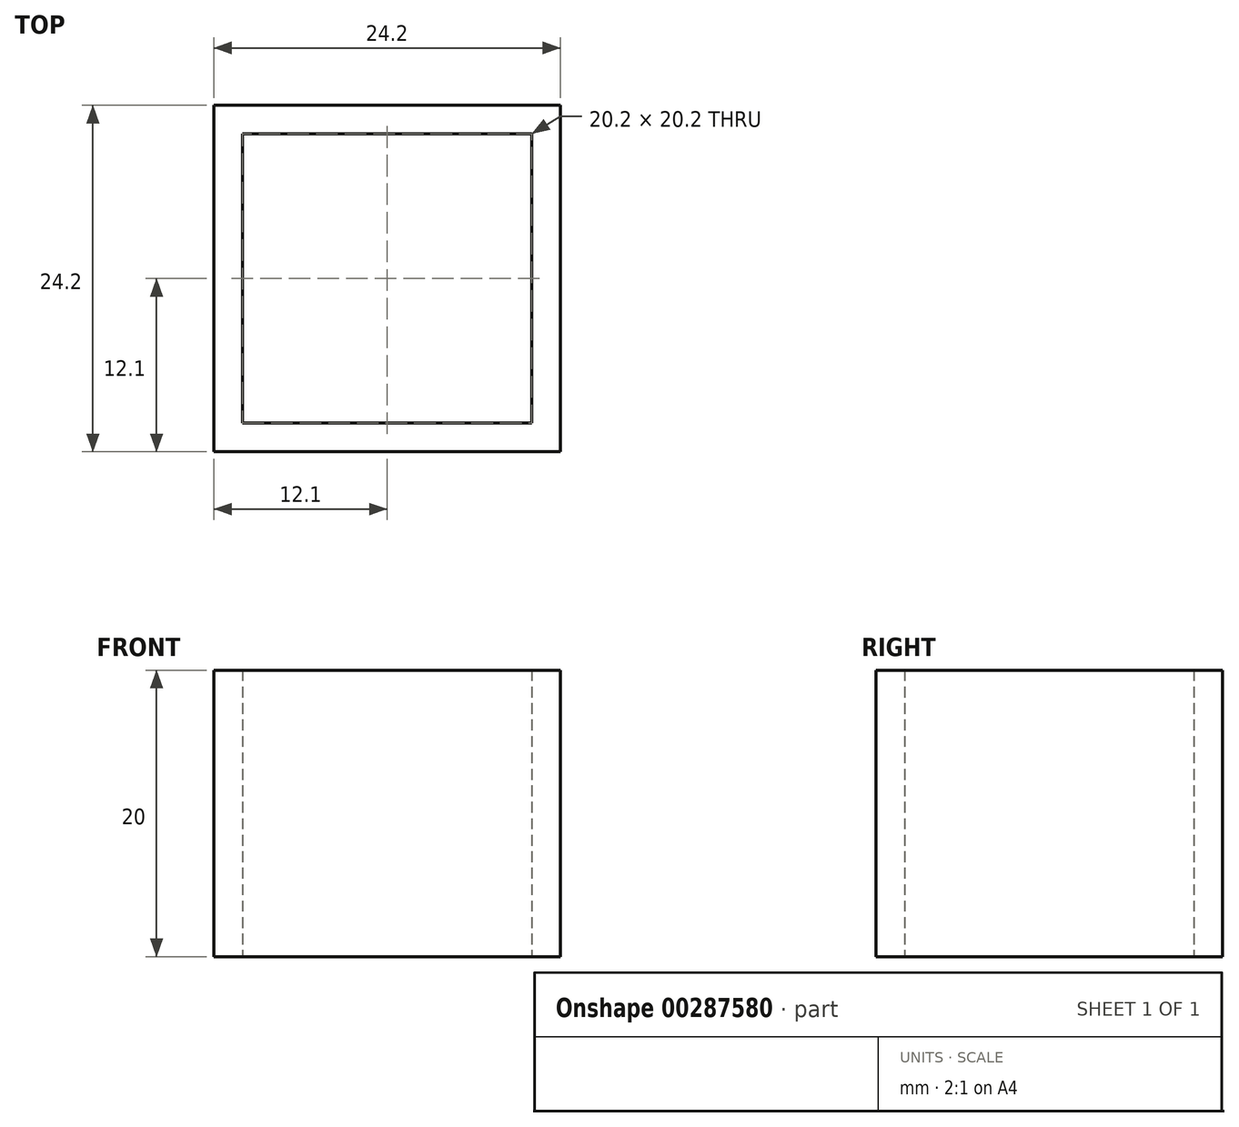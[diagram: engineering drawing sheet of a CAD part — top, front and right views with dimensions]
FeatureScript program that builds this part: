
annotation { "Feature Type Name" : "Feature", "Feature Type Description" : "" }
export const myFeature = defineFeature(function(context is Context, id is Id, definition is map)
    precondition{}
    {
        {
            var Q0;
            Q0=qCreatedBy(makeId("Top.planeOp"),FACE);
            var sketch = newSketch(context, id + "F0", { "sketchPlane" : qUnion([Q0])});
            skLineSegment(sketch, "E0.bottom", {"start": v(10.1, -10.1) * mm, "end": v(-10.1, -10.1) * mm});
            skLineSegment(sketch, "E0.top", {"start": v(10.1, 10.1) * mm, "end": v(-10.1, 10.1) * mm});
            skLineSegment(sketch, "E0.left", {"start": v(10.1, -10.1) * mm, "end": v(10.1, 10.1) * mm});
            skLineSegment(sketch, "E0.right", {"start": v(-10.1, -10.1) * mm, "end": v(-10.1, 10.1) * mm});
            skPoint(sketch, "E0.middle", {"position": v(0, 0) * mm});
            skLineSegment(sketch, "E1.bottom", {"start": v(12.1, -12.1) * mm, "end": v(-12.1, -12.1) * mm});
            skLineSegment(sketch, "E1.top", {"start": v(12.1, 12.1) * mm, "end": v(-12.1, 12.1) * mm});
            skLineSegment(sketch, "E1.left", {"start": v(12.1, -12.1) * mm, "end": v(12.1, 12.1) * mm});
            skLineSegment(sketch, "E1.right", {"start": v(-12.1, -12.1) * mm, "end": v(-12.1, 12.1) * mm});
            skSolve(sketch);
        }
        {
            var Q0;
            Q0 = qSketchRegion(id + "F0", true);
            extrude(context, id + "F1", {"entities" : qUnion([Q0]), "depth" : 20 * mm, "offsetDistance" : 25 * mm});
        }
    });
